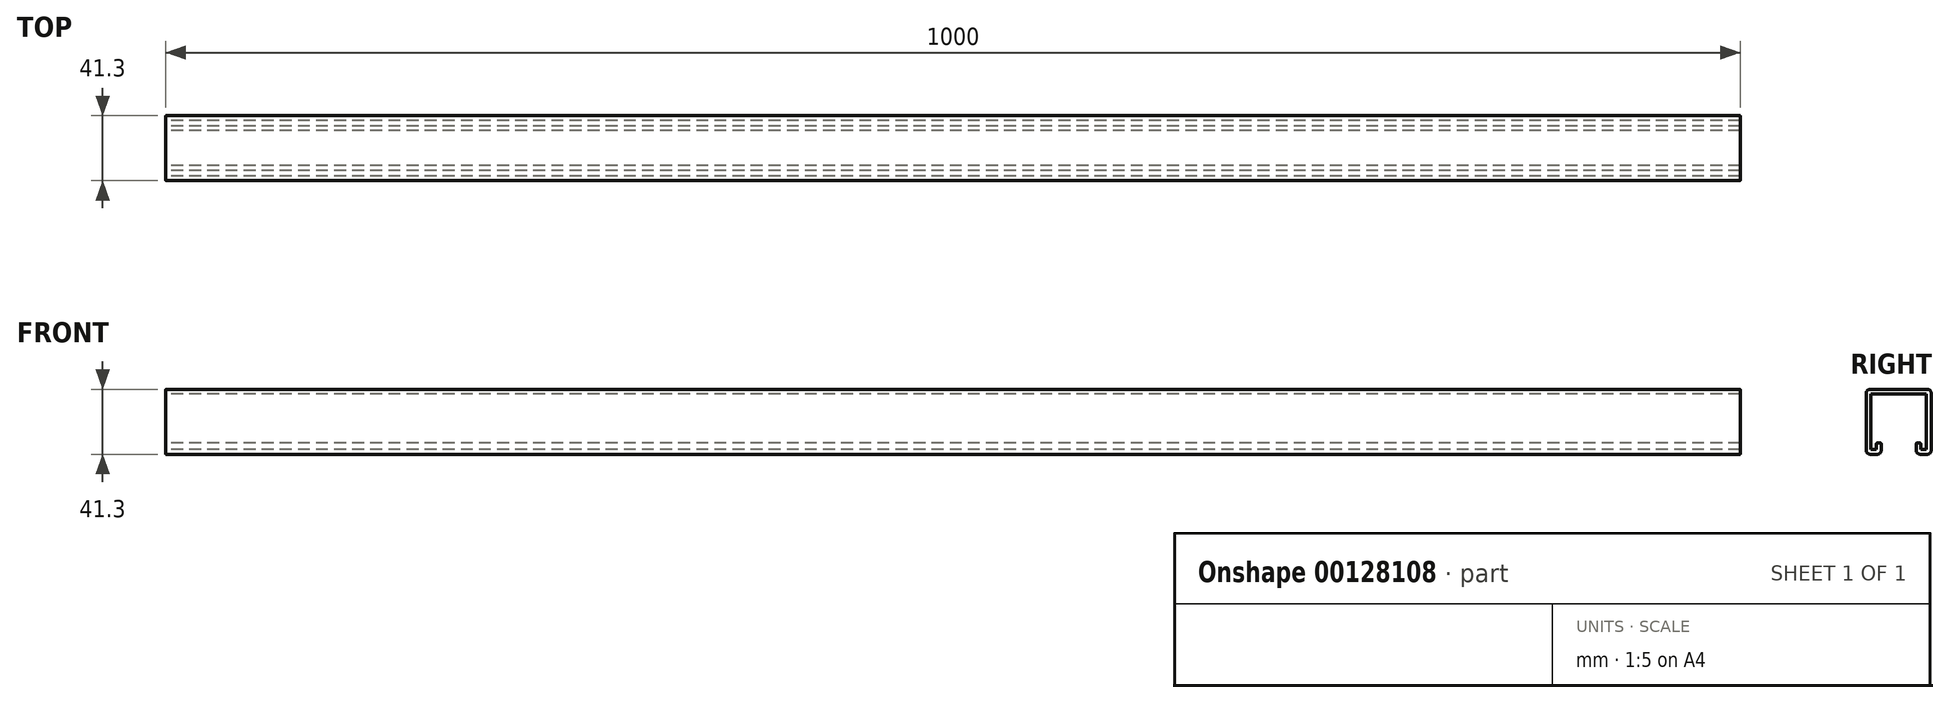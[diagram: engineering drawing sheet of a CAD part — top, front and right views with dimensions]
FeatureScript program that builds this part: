
annotation { "Feature Type Name" : "Feature", "Feature Type Description" : "" }
export const myFeature = defineFeature(function(context is Context, id is Id, definition is map)
    precondition{}
    {
        {
            var Q0;
            Q0=qCreatedBy(makeId("Right.planeOp"),FACE);
            var sketch = newSketch(context, id + "F0", { "sketchPlane" : qUnion([Q0])});
            skLineSegment(sketch, "E0", {"start": v(0, 2.5) * mm, "end": v(0, 38.8) * mm});
            skLineSegment(sketch, "E1", {"start": v(2.5, 41.3) * mm, "end": v(38.8, 41.3) * mm});
            skLineSegment(sketch, "E2", {"start": v(41.3, 38.8) * mm, "end": v(41.3, 2.5) * mm});
            skLineSegment(sketch, "E3", {"start": v(2.5, 0) * mm, "end": v(7.05, 0) * mm});
            skLineSegment(sketch, "E4", {"start": v(38.8, 0) * mm, "end": v(34.25, 0) * mm});
            skLineSegment(sketch, "E5", {"start": v(9.55, 2.5) * mm, "end": v(9.55, 6.6) * mm});
            skLineSegment(sketch, "E6", {"start": v(31.75, 2.5) * mm, "end": v(31.75, 6.6) * mm});
            skLineSegment(sketch, "E7.0", {"start": v(38.3, 38.3) * mm, "end": v(38.3, 3) * mm});
            skLineSegment(sketch, "E7.1", {"start": v(3, 38.3) * mm, "end": v(38.3, 38.3) * mm});
            skLineSegment(sketch, "E7.2", {"start": v(3, 3) * mm, "end": v(3, 38.3) * mm});
            skLineSegment(sketch, "E8.0", {"start": v(3, 3) * mm, "end": v(6.55, 3) * mm});
            skLineSegment(sketch, "E9.0", {"start": v(6.55, 3) * mm, "end": v(6.55, 6.6) * mm});
            skLineSegment(sketch, "E10.0", {"start": v(34.75, 3) * mm, "end": v(34.75, 6.6) * mm});
            skLineSegment(sketch, "E11", {"start": v(34.75, 3) * mm, "end": v(38.3, 3) * mm});
            skLineSegment(sketch, "E12", {"start": v(7.05, 7.1) * mm, "end": v(9.05, 7.1) * mm});
            skLineSegment(sketch, "E13", {"start": v(32.25, 7.1) * mm, "end": v(34.25, 7.1) * mm});
            skPoint(sketch, "E14.visualSharp", {"position": v(0, 41.3) * mm});
            skArc(sketch, "E14.filletArc", {"start": v(2.5, 41.3) * mm, "mid": v(0.73, 40.57) * mm, "end": v(0, 38.8) * mm});
            skPoint(sketch, "E15.visualSharp", {"position": v(41.3, 41.3) * mm});
            skArc(sketch, "E15.filletArc", {"start": v(41.3, 38.8) * mm, "mid": v(40.57, 40.57) * mm, "end": v(38.8, 41.3) * mm});
            skPoint(sketch, "E16.visualSharp", {"position": v(41.3, 0) * mm});
            skArc(sketch, "E16.filletArc", {"start": v(38.8, 0) * mm, "mid": v(40.57, 0.73) * mm, "end": v(41.3, 2.5) * mm});
            skPoint(sketch, "E17.visualSharp", {"position": v(0, 0) * mm});
            skArc(sketch, "E17.filletArc", {"start": v(0, 2.5) * mm, "mid": v(0.73, 0.73) * mm, "end": v(2.5, 0) * mm});
            skPoint(sketch, "E18.visualSharp", {"position": v(9.55, 0) * mm});
            skArc(sketch, "E18.filletArc", {"start": v(7.05, 0) * mm, "mid": v(8.82, 0.73) * mm, "end": v(9.55, 2.5) * mm});
            skPoint(sketch, "E19.visualSharp", {"position": v(31.75, 0) * mm});
            skArc(sketch, "E19.filletArc", {"start": v(31.75, 2.5) * mm, "mid": v(32.48, 0.73) * mm, "end": v(34.25, 0) * mm});
            skPoint(sketch, "E20.visualSharp", {"position": v(9.55, 7.1) * mm});
            skArc(sketch, "E20.filletArc", {"start": v(9.55, 6.6) * mm, "mid": v(9.4, 6.95) * mm, "end": v(9.05, 7.1) * mm});
            skPoint(sketch, "E21.visualSharp", {"position": v(6.55, 7.1) * mm});
            skArc(sketch, "E21.filletArc", {"start": v(7.05, 7.1) * mm, "mid": v(6.7, 6.95) * mm, "end": v(6.55, 6.6) * mm});
            skPoint(sketch, "E22.visualSharp", {"position": v(31.75, 7.1) * mm});
            skArc(sketch, "E22.filletArc", {"start": v(32.25, 7.1) * mm, "mid": v(31.9, 6.95) * mm, "end": v(31.75, 6.6) * mm});
            skPoint(sketch, "E23.visualSharp", {"position": v(34.75, 7.1) * mm});
            skArc(sketch, "E23.filletArc", {"start": v(34.75, 6.6) * mm, "mid": v(34.6, 6.95) * mm, "end": v(34.25, 7.1) * mm});
            skSolve(sketch);
        }
        {
            var Q0;
            Q0 = qSketchRegion(id + "F0", true);
            extrude(context, id + "F1", {"entities" : qUnion([Q0]), "depth" : 1000 * mm});
        }
    });
